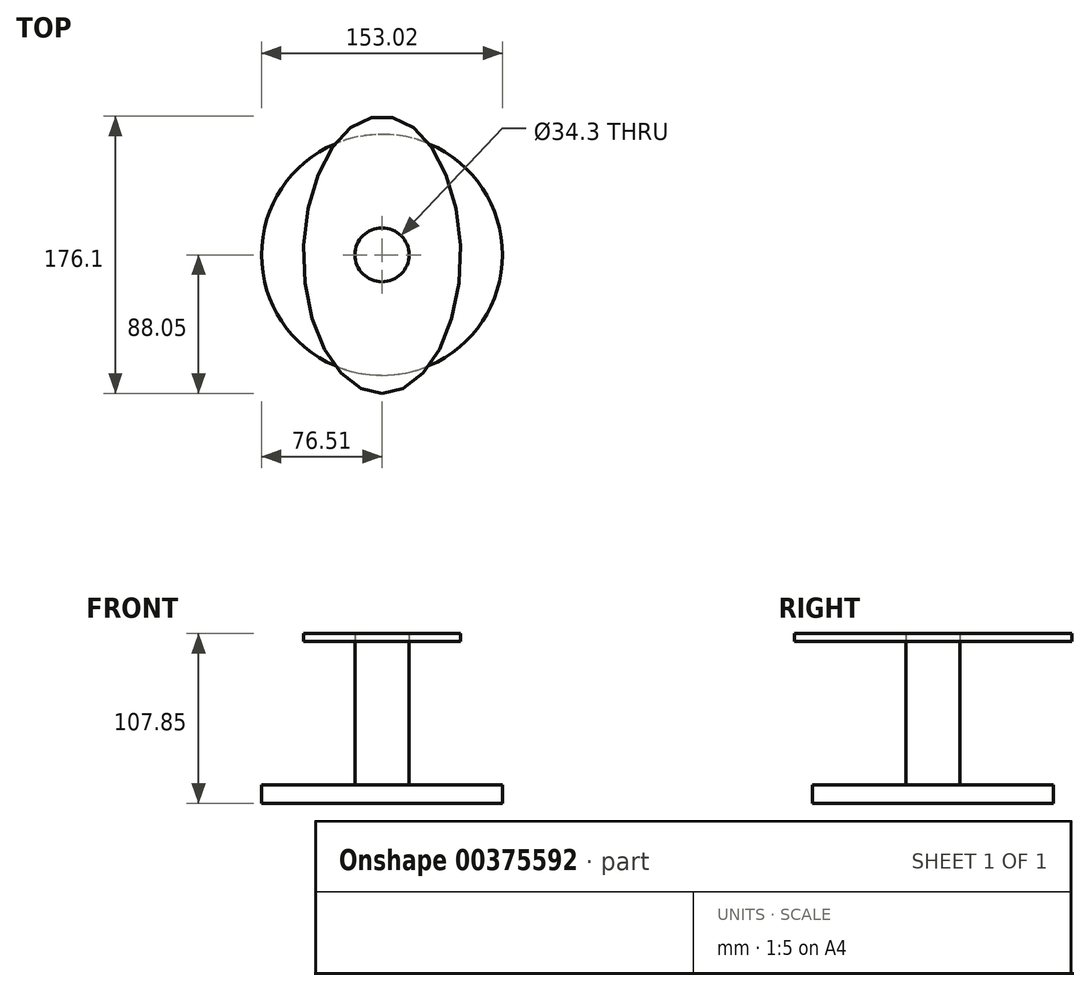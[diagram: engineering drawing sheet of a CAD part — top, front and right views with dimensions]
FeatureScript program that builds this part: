
annotation { "Feature Type Name" : "Feature", "Feature Type Description" : "" }
export const myFeature = defineFeature(function(context is Context, id is Id, definition is map)
    precondition{}
    {
        {
            var Q0;
            Q0=qCreatedBy(makeId("Top.planeOp"),FACE);
            var sketch = newSketch(context, id + "F0", { "sketchPlane" : qUnion([Q0])});
            skCircle(sketch, "E0", {"center": v(0, 0) * mm, "radius": 76.5 * mm});
            skSolve(sketch);
        }
        {
            var Q0;
            Q0 = qSketchRegion(id + "F0", true);
            extrude(context, id + "F1", {"entities" : qUnion([Q0]), "depth" : 11.75 * mm});
        }
        {
            var Q0;
            Q0=makeQuery(id+"F1.opExtrude","CAP_FACE",FACE,{"disambiguationData":[OSD([sQuery(id+"F0.wireOp",EDGE,"E0")])],"isStart":false});
            var sketch = newSketch(context, id + "F2", { "sketchPlane" : qUnion([Q0])});
            skCircle(sketch, "E1", {"center": v(0, 0) * mm, "radius": 17.15 * mm});
            skSolve(sketch);
        }
        {
            var Q0;
            Q0 = qSketchRegion(id + "F2", true);
            extrude(context, id + "F3", {"entities" : qUnion([Q0]), "operationType" : NewBodyOperationType.ADD, "depth" : 91.13 * mm});
        }
        {
            var Q0;
            Q0=makeQuery(id+"F3.opExtrude","CAP_FACE",FACE,{"disambiguationData":[OSD([sQuery(id+"F2.wireOp",EDGE,"E1")])],"isStart":false});
            var sketch = newSketch(context, id + "F4", { "sketchPlane" : qUnion([Q0])});
            skSolve(sketch);
        }
        {
            var Q0;
            Q0=makeQuery(id+"F4.imprint","IMPRINT",FACE,{"disambiguationData":[TD([[makeQuery(id+"F4.imprint","IMPRINT",EDGE,{"derivedFrom":makeQuery(id+"F3.opExtrude","CAP_EDGE",EDGE,{"disambiguationData":[OSD([sQuery(id+"F2.wireOp",EDGE,"E1")])],"isStart":false})}),1.0]])]});
            var sketch = newSketch(context, id + "F5", { "sketchPlane" : qUnion([Q0])});
            skEllipse(sketch, "E2", {"center": v(0, 0) * mm, "majorRadius": 88.05 * mm, "minorRadius": 49.88 * mm, "majorAxis": v(0, -1)});
            skSolve(sketch);
        }
        {
            var Q0;
            Q0=makeQuery(id+"F5.imprint","IMPRINT",FACE,{"disambiguationData":[TD([[makeQuery(id+"F5.imprint","IMPRINT",EDGE,{"derivedFrom":sQuery(id+"F5.wireOp",EDGE,"E2")}),1.0]])]});
            extrude(context, id + "F6", {"entities" : qUnion([Q0]), "depth" : 4.97 * mm});
        }
    });
